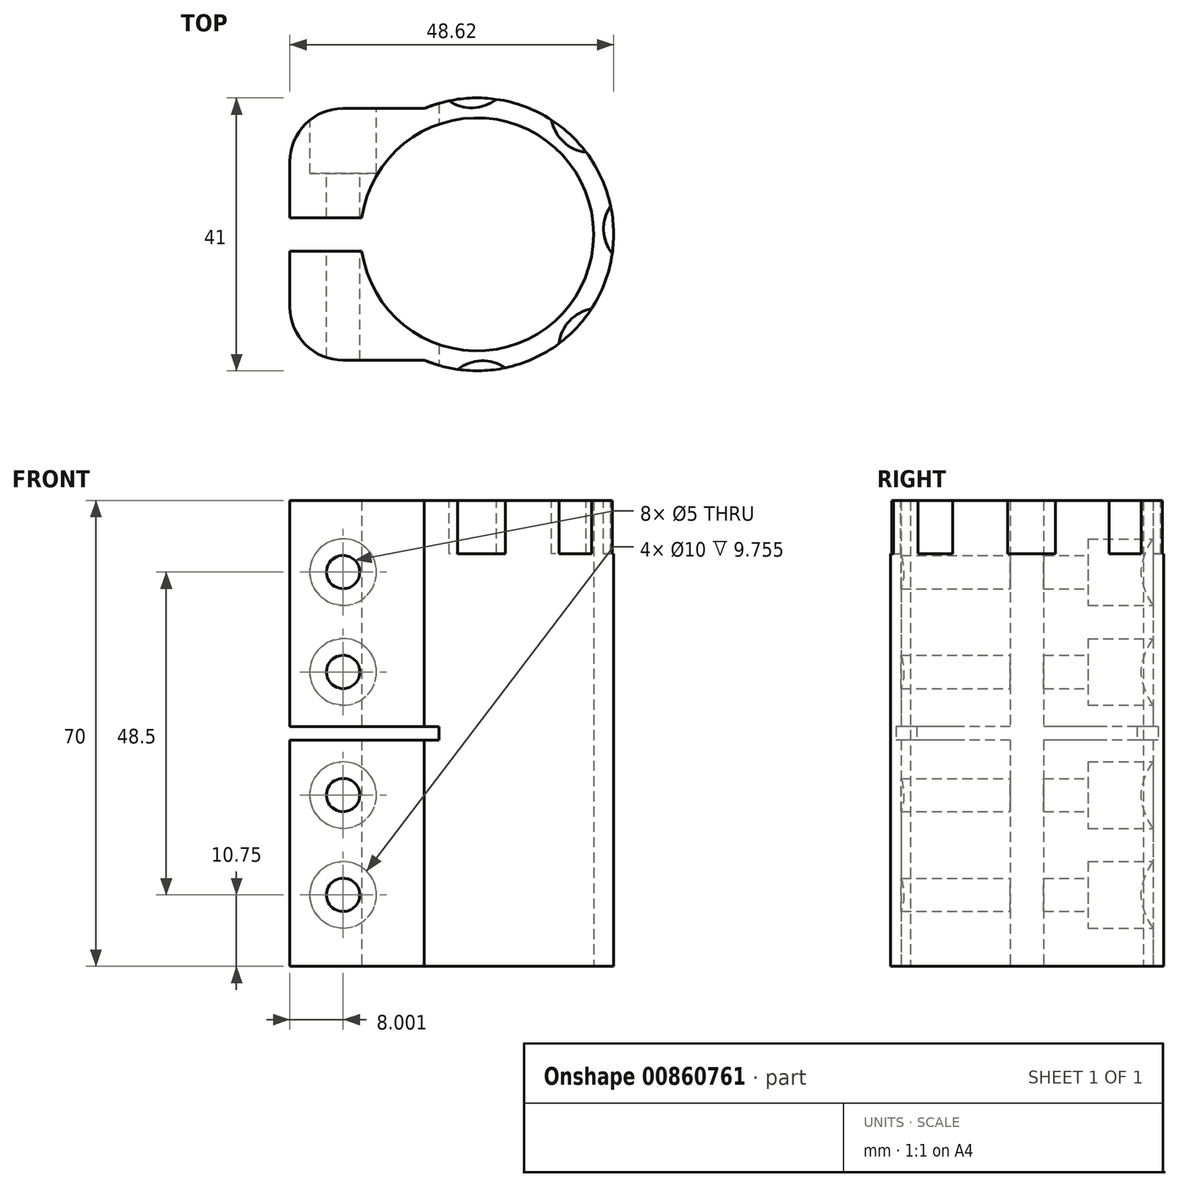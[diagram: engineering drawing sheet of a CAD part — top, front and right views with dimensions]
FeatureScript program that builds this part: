
annotation { "Feature Type Name" : "Feature", "Feature Type Description" : "" }
export const myFeature = defineFeature(function(context is Context, id is Id, definition is map)
    precondition{}
    {
        {
            var Q0;
            Q0=qCreatedBy(makeId("Top.planeOp"),FACE);
            var sketch = newSketch(context, id + "F0", { "sketchPlane" : qUnion([Q0])});
            skArc(sketch, "E0", {"start": v(-17.32, -2.5) * mm, "mid": v(17.5, 0) * mm, "end": v(-17.32, 2.5) * mm});
            skArc(sketch, "E1", {"start": v(-20.35, -2.5) * mm, "mid": v(17.73, -10.29) * mm, "end": v(-7.92, 18.9) * mm});
            skLineSegment(sketch, "E2", {"start": v(-7.92, 18.9) * mm, "end": v(-20.12, 18.9) * mm});
            skLineSegment(sketch, "E3", {"start": v(-28.12, 10.9) * mm, "end": v(-28.12, 2.5) * mm});
            skLineSegment(sketch, "E4", {"start": v(-28.12, 2.5) * mm, "end": v(-17.32, 2.5) * mm});
            skPoint(sketch, "E5.visualSharp", {"position": v(-28.12, 18.9) * mm});
            skArc(sketch, "E5.filletArc", {"start": v(-20.12, 18.9) * mm, "mid": v(-25.78, 16.57) * mm, "end": v(-28.12, 10.9) * mm});
            skLineSegment(sketch, "E6", {"start": v(0, 0) * mm, "end": v(55.32, 0) * mm, "construction": true});
            skLineSegment(sketch, "E7.MirrorCS", {"start": v(-28.12, -2.5) * mm, "end": v(-17.32, -2.5) * mm});
            skLineSegment(sketch, "E8.MirrorCS", {"start": v(-28.12, -10.9) * mm, "end": v(-28.12, -2.5) * mm});
            skArc(sketch, "E9.MirrorCS", {"start": v(-20.12, -18.9) * mm, "mid": v(-25.78, -16.57) * mm, "end": v(-28.12, -10.9) * mm});
            skLineSegment(sketch, "E10.MirrorCS", {"start": v(-7.92, -18.9) * mm, "end": v(-20.12, -18.9) * mm});
            skSolve(sketch);
        }
        {
            var Q0;
            {var subQ5=sQuery(id+"F0.wireOp",EDGE,"E0");Q0=makeQuery(id+"F0.imprint","IMPRINT",FACE,{"disambiguationData":[TD([[makeQuery(id+"F0.imprint","IMPRINT",EDGE,{"derivedFrom":subQ5}),-1.0]])]});}
            var Q1;
            {var subQ0=sQuery(id+"F0.wireOp",EDGE,"E8.MirrorCS");Q1=makeQuery(id+"F0.imprint","IMPRINT",FACE,{"disambiguationData":[TD([[makeQuery(id+"F0.imprint","IMPRINT",EDGE,{"derivedFrom":subQ0}),-1.0]])]});}
            extrude(context, id + "F1", {"entities" : qUnion([Q0, Q1]), "endBound" : BoundingType.SYMMETRIC, "depth" : 70 * mm, "offsetDistance" : 25 * mm});
        }
        {
            var Q0;
            Q0=makeQuery(id+"F1.opExtrude","SWEPT_FACE",FACE,{"disambiguationData":[OSD([sQuery(id+"F0.wireOp",EDGE,"E2")])]});
            var sketch = newSketch(context, id + "F2", { "sketchPlane" : qUnion([Q0])});
            skPoint(sketch, "E11", {"position": v(20.12, 24.25) * mm});
            skPoint(sketch, "E12", {"position": v(20.12, 9.25) * mm});
            skPoint(sketch, "E13", {"position": v(20.12, -9.25) * mm});
            skPoint(sketch, "E14", {"position": v(20.12, -24.25) * mm});
            skSolve(sketch);
        }
        {
            var Q0;
            Q0=sQuery(id+"F2.wireOp",VERTEX,"E11");
            var Q1;
            Q1=sQuery(id+"F2.wireOp",VERTEX,"E12");
            var Q2;
            Q2=sQuery(id+"F2.wireOp",VERTEX,"E13");
            var Q3;
            Q3=sQuery(id+"F2.wireOp",VERTEX,"E14");
            var Q4;
            Q4=makeQuery(id+"F1.opExtrude","SWEPT_BODY",BODY,{"disambiguationData":[OSD([sQuery(id+"F0.wireOp",EDGE,"E0"),sQuery(id+"F0.wireOp",EDGE,"E1"),sQuery(id+"F0.wireOp",EDGE,"E2"),sQuery(id+"F0.wireOp",EDGE,"E3"),sQuery(id+"F0.wireOp",EDGE,"E4"),sQuery(id+"F0.wireOp",EDGE,"E5.filletArc"),sQuery(id+"F0.wireOp",EDGE,"E7.MirrorCS"),sQuery(id+"F0.wireOp",EDGE,"E8.MirrorCS"),sQuery(id+"F0.wireOp",EDGE,"E9.MirrorCS"),sQuery(id+"F0.wireOp",EDGE,"E10.MirrorCS")])]});
            hole(context, id + "F3", {"style" : HoleStyle.C_BORE, "endStyle" : HoleEndStyle.THROUGH, "holeDiameter" : 5 * mm, "cBoreDiameter" : 10 * mm, "cBoreDepth" : 8 * mm, "majorDiameter" : 5 * mm, "isTappedThrough" : true, "tappedDepth" : 12 * mm, "tapClearance" : 3, "locations" : qUnion([Q0, Q1, Q2, Q3]), "scope" : qUnion([Q4])});
        }
        {
            var Q0;
            Q0=qCreatedBy(makeId("Front.planeOp"),FACE);
            var sketch = newSketch(context, id + "F4", { "sketchPlane" : qUnion([Q0])});
            skLineSegment(sketch, "E15.bottom", {"start": v(-5.72, 1) * mm, "end": v(-28.12, 1) * mm});
            skLineSegment(sketch, "E15.top", {"start": v(-5.72, -1) * mm, "end": v(-28.12, -1) * mm});
            skLineSegment(sketch, "E15.left", {"start": v(-5.72, 1) * mm, "end": v(-5.72, -1) * mm});
            skLineSegment(sketch, "E15.right", {"start": v(-28.12, 1) * mm, "end": v(-28.12, -1) * mm});
            skSolve(sketch);
        }
        {
            var Q0;
            Q0=qSketchRegion(id+"F4",true);
            extrude(context, id + "F5", {"entities" : qUnion([Q0]), "operationType" : NewBodyOperationType.REMOVE, "endBound" : BoundingType.SYMMETRIC, "oppositeDirection" : true, "depth" : 50 * mm, "offsetDistance" : 25 * mm});
        }
        {
            var Q0;
            Q0=makeQuery(id+"F1.opExtrude","CAP_FACE",FACE,{"disambiguationData":[OSD([sQuery(id+"F0.wireOp",EDGE,"E0"),sQuery(id+"F0.wireOp",EDGE,"E1"),sQuery(id+"F0.wireOp",EDGE,"E2"),sQuery(id+"F0.wireOp",EDGE,"E3"),sQuery(id+"F0.wireOp",EDGE,"E4"),sQuery(id+"F0.wireOp",EDGE,"E5.filletArc"),sQuery(id+"F0.wireOp",EDGE,"E7.MirrorCS"),sQuery(id+"F0.wireOp",EDGE,"E8.MirrorCS"),sQuery(id+"F0.wireOp",EDGE,"E9.MirrorCS"),sQuery(id+"F0.wireOp",EDGE,"E10.MirrorCS")])],"isStart":false});
            var sketch = newSketch(context, id + "F6", { "sketchPlane" : qUnion([Q0])});
            skCircle(sketch, "E16", {"center": v(0.83, -25) * mm, "radius": 6 * mm});
            skCircle(sketch, "E17.1.0", {"center": v(18.26, -17.1) * mm, "radius": 6 * mm});
            skCircle(sketch, "E17.2.0", {"center": v(25, 0.83) * mm, "radius": 6 * mm});
            skCircle(sketch, "E17.3.0", {"center": v(17.1, 18.26) * mm, "radius": 6 * mm});
            skCircle(sketch, "E17.4.0", {"center": v(-0.83, 25) * mm, "radius": 6 * mm});
            skPoint(sketch, "E17.center", {"position": v(0, 0) * mm});
            skLineSegment(sketch, "E17.anchor1", {"start": v(0, 0) * mm, "end": v(0.83, -25) * mm, "construction": true});
            skLineSegment(sketch, "E17.anchor2", {"start": v(0, 0) * mm, "end": v(-0.83, 25) * mm, "construction": true});
            skSolve(sketch);
        }
        {
            var Q0;
            Q0=qSketchRegion(id+"F6",true);
            extrude(context, id + "F7", {"entities" : qUnion([Q0]), "operationType" : NewBodyOperationType.REMOVE, "oppositeDirection" : true, "depth" : 8 * mm, "offsetDistance" : 25 * mm});
        }
    });
